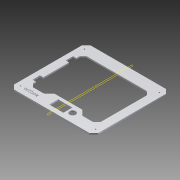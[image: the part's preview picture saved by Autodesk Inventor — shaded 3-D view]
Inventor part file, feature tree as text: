
AUTODESK INVENTOR PART (.ipt)
format: ipt  version: 2015 (Build 190159000, 159)  size: 877,568 bytes
history: native  units: mm
features: extrude x7, fillet x3, hole x1, chamfer x1, projected_geometry x1
ambient origin geometry x8: Origin, YZ Plane, XZ Plane, XY Plane, X Axis, Y Axis, Z Axis, Center Point
bodies: Solid1 (feature_tree)
feature tree (13):
  extrude  "Extrusión1"  Depth=480.0mm
  fillet  "Empalme1"  Radius=436.5mm
  extrude  "Extrusión3"  Depth=385.0mm
  extrude  "Extrusión6"  Depth=65.0mm
  fillet  "Empalme2"  Radius=8.0mm
  extrude  "Extrusión7"  Depth=20.0mm
  hole  "Agujero1"  [1 undecoded]
  extrude  "AGUJERO BEEPER"  Depth=10.0mm
  extrude  "RANURA ACOPLAMIENTO"  Depth=81.0mm
  fillet  "Empalme3"  Radius=51.0mm
  chamfer  "Chaflán5"  Distance=10.0mm
  extrude  "Extrusión11"  Depth=35.0mm
  projected_geometry  "Contorno proyectado1"
note: 1 required parameter value undecoded (feature->parameter linkage not recoverable at this tier; creation-order binding heuristic only, values carry confidence <= 0.55)
